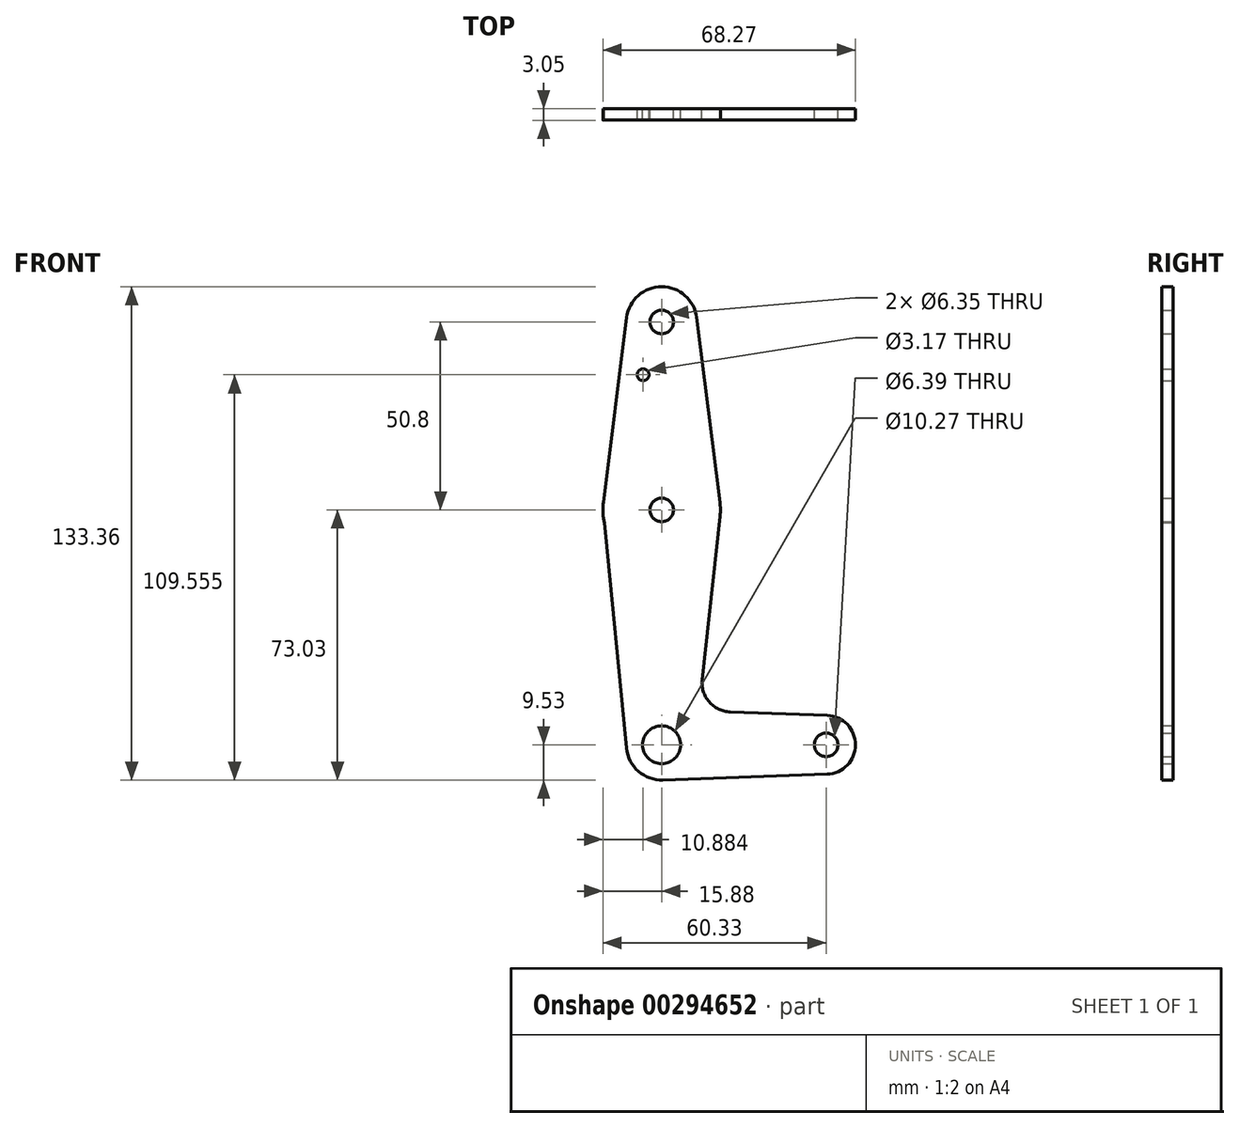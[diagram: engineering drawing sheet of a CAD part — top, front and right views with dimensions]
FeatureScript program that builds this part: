
annotation { "Feature Type Name" : "Feature", "Feature Type Description" : "" }
export const myFeature = defineFeature(function(context is Context, id is Id, definition is map)
    precondition{}
    {
        {
            var Q0;
            Q0=qCreatedBy(makeId("Front.planeOp"),FACE);
            var sketch = newSketch(context, id + "F0", { "sketchPlane" : qUnion([Q0])});
            skLineSegment(sketch, "E0", {"start": v(0, 0) * mm, "end": v(0, 63.5) * mm, "construction": true});
            skLineSegment(sketch, "E1", {"start": v(0, 63.5) * mm, "end": v(0, 114.3) * mm, "construction": true});
            skCircle(sketch, "E2", {"center": v(0, 0) * mm, "radius": 9.53 * mm});
            skCircle(sketch, "E3", {"center": v(0, 114.3) * mm, "radius": 9.53 * mm});
            skCircle(sketch, "E4", {"center": v(0, 63.5) * mm, "radius": 15.88 * mm});
            skLineSegment(sketch, "E5", {"start": v(0, 0) * mm, "end": v(44.45, 0) * mm, "construction": true});
            skCircle(sketch, "E6", {"center": v(44.45, 0) * mm, "radius": 7.94 * mm});
            skLineSegment(sketch, "E7", {"start": v(18.56, 8.87) * mm, "end": v(44.73, 7.93) * mm});
            skLineSegment(sketch, "E8", {"start": v(0.34, -9.52) * mm, "end": v(44.73, -7.93) * mm});
            skLineSegment(sketch, "E9", {"start": v(-9.45, 115.5) * mm, "end": v(-15.75, 65.48) * mm});
            skLineSegment(sketch, "E10", {"start": v(9.45, 115.5) * mm, "end": v(15.75, 65.48) * mm});
            skCircle(sketch, "E11", {"center": v(0, 114.3) * mm, "radius": 3.18 * mm});
            skCircle(sketch, "E12", {"center": v(-5, 100.03) * mm, "radius": 1.59 * mm});
            skCircle(sketch, "E13", {"center": v(0, 63.5) * mm, "radius": 3.18 * mm});
            skCircle(sketch, "E14", {"center": v(0, 0) * mm, "radius": 5.13 * mm});
            skCircle(sketch, "E15", {"center": v(44.45, 0) * mm, "radius": 3.2 * mm});
            skLineSegment(sketch, "E16", {"start": v(-15.5, 60.06) * mm, "end": v(-9.48, -0.94) * mm});
            skLineSegment(sketch, "E17", {"start": v(15.78, 61.77) * mm, "end": v(10.94, 17.68) * mm});
            skArc(sketch, "E18.filletArc", {"start": v(10.94, 17.68) * mm, "mid": v(12.83, 11.61) * mm, "end": v(18.56, 8.87) * mm});
            skSolve(sketch);
        }
        {
            var Q0;
            Q0 = qSketchRegion(id + "F0", true);
            extrude(context, id + "F1", {"entities" : qUnion([Q0]), "depth" : 3.05 * mm});
        }
    });
